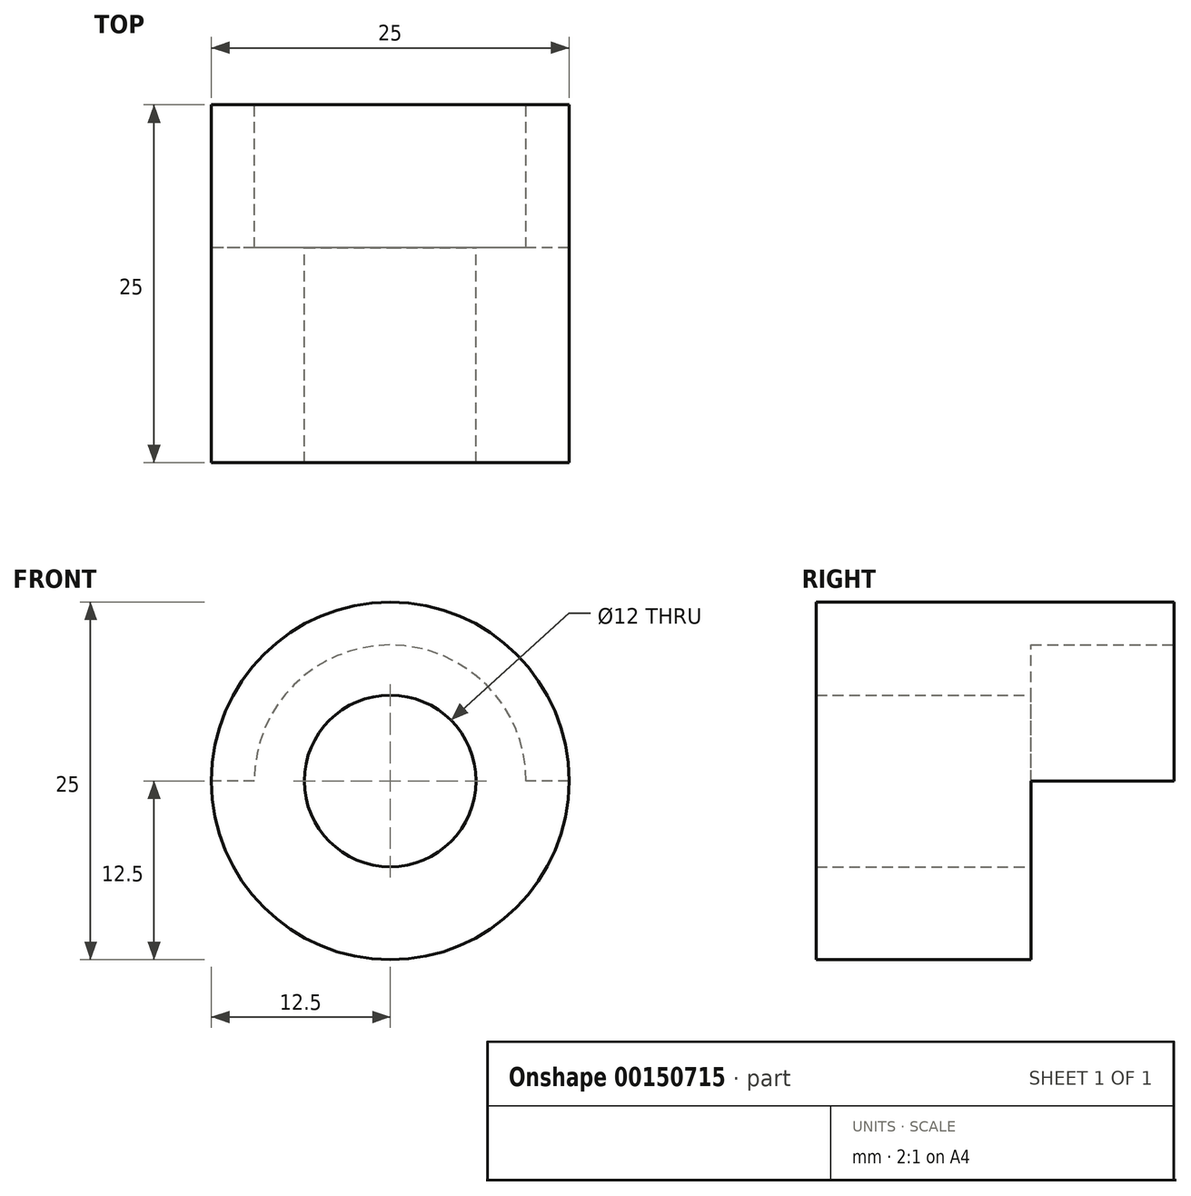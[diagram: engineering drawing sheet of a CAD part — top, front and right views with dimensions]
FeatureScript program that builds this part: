
annotation { "Feature Type Name" : "Feature", "Feature Type Description" : "" }
export const myFeature = defineFeature(function(context is Context, id is Id, definition is map)
    precondition{}
    {
        {
            var Q0;
            Q0=qCreatedBy(makeId("Front.planeOp"),FACE);
            var sketch = newSketch(context, id + "F0", { "sketchPlane" : qUnion([Q0])});
            skCircle(sketch, "E0", {"center": v(0, 0) * mm, "radius": 12.5 * mm});
            skCircle(sketch, "E1", {"center": v(0, 0) * mm, "radius": 6 * mm});
            skSolve(sketch);
        }
        {
            var Q0;
            Q0 = qSketchRegion(id + "F0", true);
            extrude(context, id + "F1", {"entities" : qUnion([Q0]), "depth" : 25 * mm});
        }
        {
            var Q0;
            Q0=qCreatedBy(makeId("Front.planeOp"),FACE);
            var sketch = newSketch(context, id + "F2", { "sketchPlane" : qUnion([Q0])});
            skCircle(sketch, "E2", {"center": v(0, 0) * mm, "radius": 9.5 * mm});
            skSolve(sketch);
        }
        {
            var Q0;
            Q0 = qSketchRegion(id + "F2", true);
            extrude(context, id + "F3", {"entities" : qUnion([Q0]), "operationType" : NewBodyOperationType.REMOVE, "depth" : 10 * mm});
        }
        {
            var Q0;
            Q0=makeQuery(id+"F1.opExtrude","CAP_FACE",FACE,{"disambiguationData":[OSD([sQuery(id+"F0.wireOp",EDGE,"E0"),sQuery(id+"F0.wireOp",EDGE,"E1")])],"isStart":true});
            var sketch = newSketch(context, id + "F4", { "sketchPlane" : qUnion([Q0])});
            skLineSegment(sketch, "E3.bottom", {"start": v(-17.04, 0) * mm, "end": v(15.34, 0) * mm});
            skLineSegment(sketch, "E3.top", {"start": v(-17.04, -14.5) * mm, "end": v(15.34, -14.5) * mm});
            skLineSegment(sketch, "E3.left", {"start": v(-17.04, 0) * mm, "end": v(-17.04, -14.5) * mm});
            skLineSegment(sketch, "E3.right", {"start": v(15.34, 0) * mm, "end": v(15.34, -14.5) * mm});
            skSolve(sketch);
        }
        {
            var Q0;
            Q0 = qSketchRegion(id + "F4", true);
            extrude(context, id + "F5", {"entities" : qUnion([Q0]), "operationType" : NewBodyOperationType.REMOVE, "oppositeDirection" : true, "depth" : 10 * mm});
        }
    });
